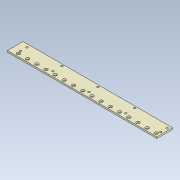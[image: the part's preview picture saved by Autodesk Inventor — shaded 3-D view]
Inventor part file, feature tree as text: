
AUTODESK INVENTOR PART (.ipt)
format: ipt  version: 2022.4 (Build 264492010, 492A)  size: 141,312 bytes
history: native  units: in
note: dims shown in document units (in); Inventor stores cm internally (conversion verified against a paired STEP export)
features: sketch x3, other x2, hole x2, extrude x1
ambient origin geometry x8: Origin, YZ Plane, XZ Plane, XY Plane, X Axis, Y Axis, Z Axis, Center Point
bodies: Solid1 (feature_tree)
feature tree (8):
  other  "main_manifold_8v_v02.ipt"
  other  "TC: base"
  extrude  "Ex: base"  [1 undecoded]
  hole  "Hole: TC screws: 4-40 through hole"  [1 undecoded]
  hole  "Hole: MMC screws: 4-40 head through hole"  [1 undecoded]
  sketch  "Sketch:MM: prop valve cutout"  dims[d5=0.224in d6=0.219in d7=0.112in d8=0.5635in d9=1.0in d10=0.8108in]
  sketch  "Sketch:MM: MMC screws"  dims[d12=0.224in d13=0.219in d14=0.112in d15=0.5635in d16=1.0in d17=0.8108in]
  sketch  "Sketch:MM: bath & TC screws"
note: 3 required parameter values undecoded (feature->parameter linkage not recoverable at this tier; creation-order binding heuristic only, values carry confidence <= 0.55)
